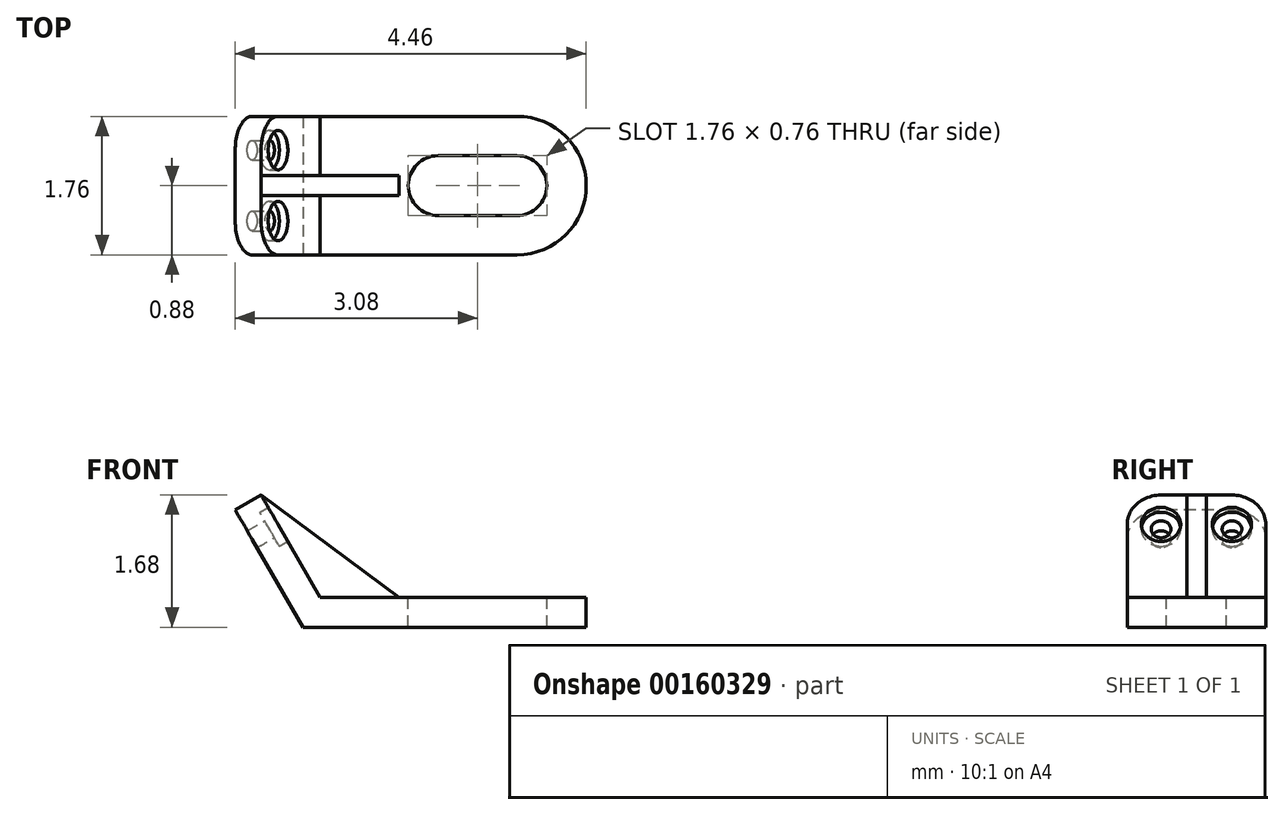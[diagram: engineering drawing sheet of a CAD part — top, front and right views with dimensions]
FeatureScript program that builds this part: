
annotation { "Feature Type Name" : "Feature", "Feature Type Description" : "" }
export const myFeature = defineFeature(function(context is Context, id is Id, definition is map)
    precondition{}
    {
        {
            var Q0;
            Q0=qCreatedBy(makeId("Front.planeOp"),FACE);
            var sketch = newSketch(context, id + "F0", { "sketchPlane" : qUnion([Q0])});
            skLineSegment(sketch, "E0", {"start": v(0, 0) * mm, "end": v(2.5, 0) * mm});
            skLineSegment(sketch, "E1", {"start": v(2.5, 0) * mm, "end": v(3.38, 0) * mm});
            skLineSegment(sketch, "E2", {"start": v(3.38, 0) * mm, "end": v(3.38, -0.38) * mm});
            skLineSegment(sketch, "E3", {"start": v(0, 0) * mm, "end": v(-0.75, 1.3) * mm});
            skLineSegment(sketch, "E4", {"start": v(-0.75, 1.3) * mm, "end": v(-1.08, 1.1) * mm});
            skLineSegment(sketch, "E5", {"start": v(-1.08, 1.1) * mm, "end": v(-0.22, -0.38) * mm});
            skLineSegment(sketch, "E6", {"start": v(3.38, -0.38) * mm, "end": v(-0.22, -0.38) * mm});
            skSolve(sketch);
        }
        {
            var Q0;
            Q0 = qSketchRegion(id + "F0", true);
            extrude(context, id + "F1", {"entities" : qUnion([Q0]), "oppositeDirection" : true, "depth" : 1.76 * mm});
        }
        {
            var Q0;
            Q0=makeQuery(id+"F1.opExtrude","SWEPT_FACE",FACE,{"disambiguationData":[OSD([sQuery(id+"F0.wireOp",EDGE,"E0"),sQuery(id+"F0.wireOp",EDGE,"E1")])]});
            var sketch = newSketch(context, id + "F2", { "sketchPlane" : qUnion([Q0])});
            skArc(sketch, "E7", {"start": v(2.5, 0) * mm, "mid": v(3.38, 0.88) * mm, "end": v(2.5, 1.76) * mm});
            skLineSegment(sketch, "E8", {"start": v(2.5, 0.88) * mm, "end": v(1.5, 0.88) * mm, "construction": true});
            skArc(sketch, "E9", {"start": v(2.5, 0.5) * mm, "mid": v(2.88, 0.88) * mm, "end": v(2.5, 1.26) * mm});
            skLineSegment(sketch, "E10", {"start": v(2.5, 1.26) * mm, "end": v(1.5, 1.26) * mm});
            skArc(sketch, "E11", {"start": v(1.5, 1.26) * mm, "mid": v(1.12, 0.88) * mm, "end": v(1.5, 0.5) * mm});
            skLineSegment(sketch, "E12", {"start": v(1.5, 0.5) * mm, "end": v(2.5, 0.5) * mm});
            skSolve(sketch);
        }
        {
            var Q0;
            Q0 = qSketchRegion(id + "F2", true);
            var Q1;
            {var subQ0=sQuery(id+"F2.wireOp",EDGE,"E7");var subQ1=sQuery(id+"F0.wireOp",EDGE,"E1");var subQ2=makeQuery(id+"F1.opExtrude","CAP_EDGE",EDGE,{"disambiguationData":[OSD([sQuery(id+"F0.wireOp",EDGE,"E0"),subQ1])],"isStart":false});var subQ3=makeQuery(id+"F2.imprint","INTERSECT",VERTEX,{"derivedFrom":[subQ2,subQ0]});Q1=makeQuery(id+"F2.imprint","IMPRINT",FACE,{"disambiguationData":[TD([[makeQuery(id+"F2.imprint","IMPRINT",EDGE,{"disambiguationData":[TD([[subQ3,1.0]])],"derivedFrom":subQ0}),-1.0]])]});}
            var Q2;
            {var subQ0=sQuery(id+"F2.wireOp",EDGE,"E7");var subQ1=sQuery(id+"F0.wireOp",EDGE,"E1");var subQ2=makeQuery(id+"F1.opExtrude","CAP_EDGE",EDGE,{"disambiguationData":[OSD([sQuery(id+"F0.wireOp",EDGE,"E0"),subQ1])],"isStart":true});var subQ3=makeQuery(id+"F2.imprint","INTERSECT",VERTEX,{"derivedFrom":[subQ2,subQ0]});Q2=makeQuery(id+"F2.imprint","IMPRINT",FACE,{"disambiguationData":[TD([[makeQuery(id+"F2.imprint","IMPRINT",EDGE,{"disambiguationData":[TD([[subQ3,-1.0]])],"derivedFrom":subQ0}),-1.0]])]});}
            extrude(context, id + "F3", {"entities" : qUnion([Q0, Q1, Q2]), "operationType" : NewBodyOperationType.REMOVE, "oppositeDirection" : true, "depth" : 25 * mm});
        }
        {
            var Q0;
            Q0=makeQuery(id+"F1.opExtrude","SWEPT_FACE",FACE,{"disambiguationData":[OSD([sQuery(id+"F0.wireOp",EDGE,"E3")])]});
            var sketch = newSketch(context, id + "F4", { "sketchPlane" : qUnion([Q0])});
            skArc(sketch, "E13", {"start": v(1.76, 1.07) * mm, "mid": v(1.63, 1.37) * mm, "end": v(1.33, 1.5) * mm});
            skArc(sketch, "E14", {"start": v(0.43, 1.5) * mm, "mid": v(0.13, 1.37) * mm, "end": v(0, 1.07) * mm});
            skCircle(sketch, "E15", {"center": v(0.43, 1.07) * mm, "radius": 0.25 * mm});
            skCircle(sketch, "E16", {"center": v(1.33, 1.07) * mm, "radius": 0.25 * mm});
            skSolve(sketch);
        }
        {
            var Q0;
            Q0 = qSketchRegion(id + "F4", true);
            extrude(context, id + "F5", {"entities" : qUnion([Q0]), "operationType" : NewBodyOperationType.REMOVE, "oppositeDirection" : true, "depth" : 0.12 * mm});
        }
        {
            var Q0;
            {var subQ0=sQuery(id+"F4.wireOp",EDGE,"E13");Q0=makeQuery(id+"F4.imprint","IMPRINT",FACE,{"disambiguationData":[TD([[makeQuery(id+"F4.imprint","IMPRINT",EDGE,{"derivedFrom":subQ0}),-1.0]])]});}
            var Q1;
            {var subQ0=sQuery(id+"F4.wireOp",EDGE,"E14");Q1=makeQuery(id+"F4.imprint","IMPRINT",FACE,{"disambiguationData":[TD([[makeQuery(id+"F4.imprint","IMPRINT",EDGE,{"derivedFrom":subQ0}),-1.0]])]});}
            extrude(context, id + "F6", {"entities" : qUnion([Q0, Q1]), "operationType" : NewBodyOperationType.REMOVE, "oppositeDirection" : true, "depth" : 25 * mm});
        }
        {
            var Q0;
            {var subQ3=sQuery(id+"F4.wireOp",EDGE,"E13");Q0=makeQuery(id+"F4.imprint","IMPRINT",FACE,{"disambiguationData":[TD([[makeQuery(id+"F4.imprint","IMPRINT",EDGE,{"derivedFrom":subQ3}),1.0]])]});}
            cPlane(context, id + "F7", {"entities" : qUnion([Q0]), "cplaneType" : CPlaneType.OFFSET, "offset" : 0.12 * mm, "oppositeDirection" : true, "width" : 150 * mm, "height" : 150 * mm});
        }
        {
            var Q0;
            Q0=qCreatedBy(id+"F7.planeOp",FACE);
            var sketch = newSketch(context, id + "F8", { "sketchPlane" : qUnion([Q0])});
            skPoint(sketch, "E17.0", {"position": v(0.43, 1.07) * mm});
            skCircle(sketch, "E18", {"center": v(0.43, 1.07) * mm, "radius": 0.12 * mm});
            skPoint(sketch, "E19.0", {"position": v(1.33, 1.07) * mm});
            skCircle(sketch, "E20", {"center": v(1.33, 1.07) * mm, "radius": 0.12 * mm});
            skSolve(sketch);
        }
        {
            var Q0;
            Q0 = qSketchRegion(id + "F8", true);
            extrude(context, id + "F9", {"entities" : qUnion([Q0]), "operationType" : NewBodyOperationType.REMOVE, "oppositeDirection" : true, "depth" : 25 * mm});
        }
        {
            var Q0;
            Q0=qCreatedBy(makeId("Front.planeOp"),FACE);
            cPlane(context, id + "F10", {"entities" : qUnion([Q0]), "cplaneType" : CPlaneType.OFFSET, "offset" : 0.88 * mm, "oppositeDirection" : true, "width" : 150 * mm, "height" : 150 * mm});
        }
        {
            var Q0;
            Q0=qCreatedBy(id+"F10.planeOp",FACE);
            var sketch = newSketch(context, id + "F11", { "sketchPlane" : qUnion([Q0])});
            skLineSegment(sketch, "E21", {"start": v(0, 0) * mm, "end": v(1, 0) * mm});
            skPoint(sketch, "E22.0", {"position": v(-0.75, 1.3) * mm});
            skLineSegment(sketch, "E23", {"start": v(-0.75, 1.3) * mm, "end": v(1, 0) * mm});
            skLineSegment(sketch, "E24", {"start": v(-0.75, 1.3) * mm, "end": v(0, 0) * mm});
            skSolve(sketch);
        }
        {
            var Q0;
            Q0 = qSketchRegion(id + "F11", true);
            extrude(context, id + "F12", {"entities" : qUnion([Q0]), "operationType" : NewBodyOperationType.ADD, "endBound" : BoundingType.SYMMETRIC, "depth" : 0.25 * mm});
        }
    });
